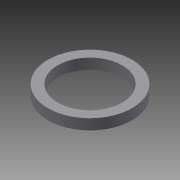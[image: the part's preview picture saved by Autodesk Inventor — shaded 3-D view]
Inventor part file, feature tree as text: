
AUTODESK INVENTOR PART (.ipt)
format: ipt  version: 2013 (Build 170138000, 138)  size: 73,216 bytes
history: native  units: in
note: dims shown in document units (in); Inventor stores cm internally (conversion verified against a paired STEP export)
features: extrude x1, sketch x1
ambient origin geometry x8: Origin, YZ Plane, XZ Plane, XY Plane, X Axis, Y Axis, Z Axis, Center Point
bodies: Solid1 (feature_tree)
feature tree (2):
  extrude  "Extrusion1"  Depth=1.0in
  sketch  "Sketch1"  dims[d0=0.768in d1=1.0in d2=0.125in d3=0.0in]
